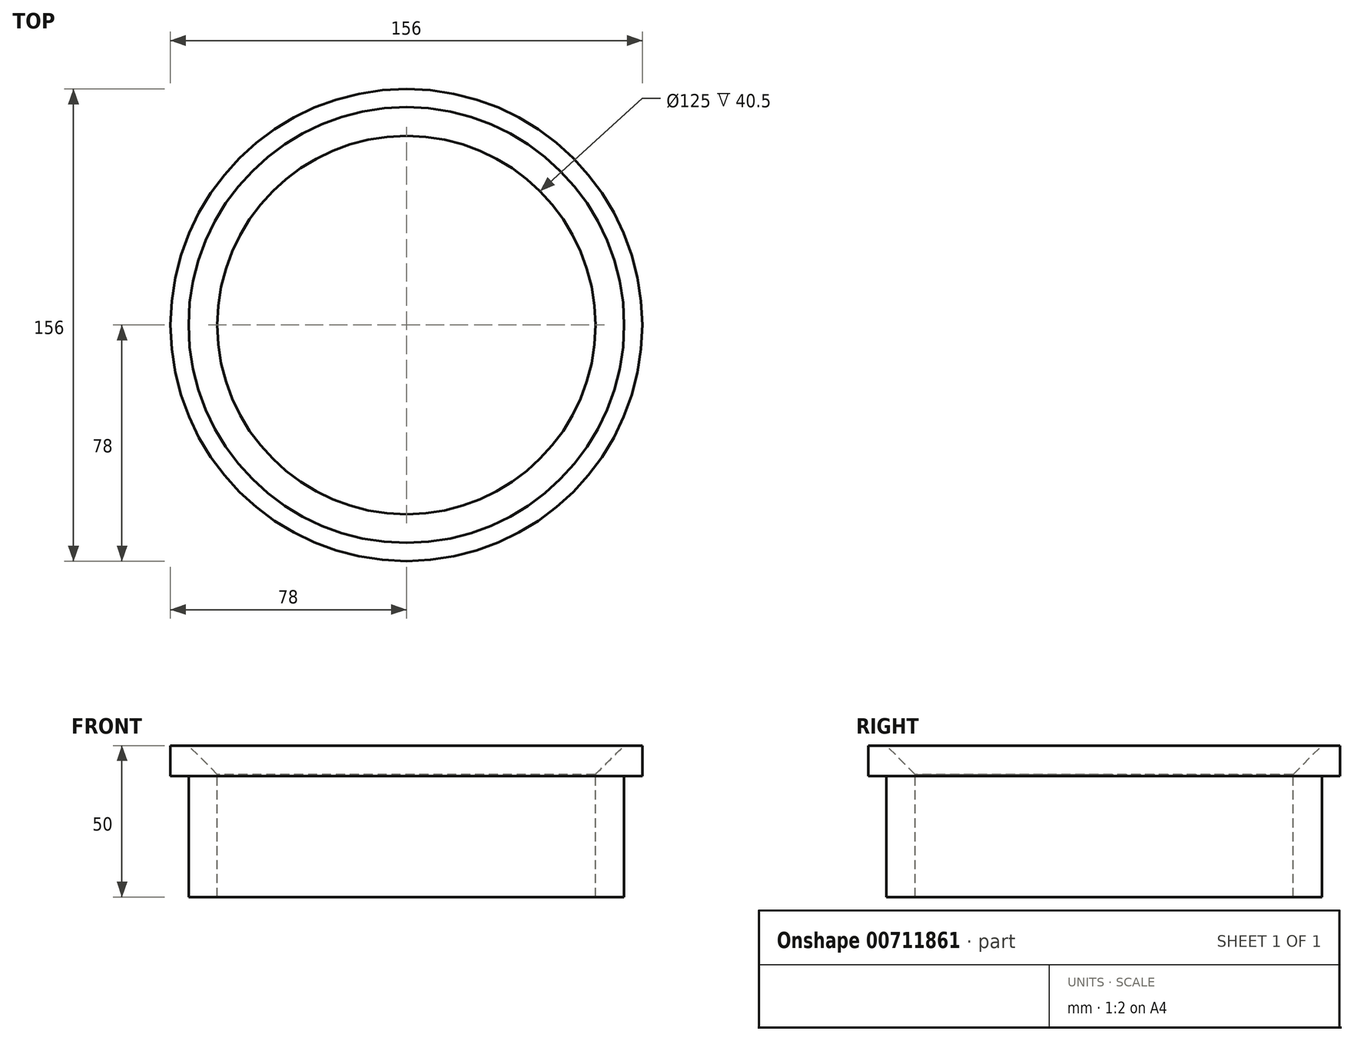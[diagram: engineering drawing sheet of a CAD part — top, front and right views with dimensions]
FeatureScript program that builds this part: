
annotation { "Feature Type Name" : "Feature", "Feature Type Description" : "" }
export const myFeature = defineFeature(function(context is Context, id is Id, definition is map)
    precondition{}
    {
        {
            var Q0;
            Q0=qCreatedBy(makeId("Front.planeOp"),FACE);
            var sketch = newSketch(context, id + "F0", { "sketchPlane" : qUnion([Q0])});
            skLineSegment(sketch, "E0", {"start": v(0, 50) * mm, "end": v(0, 0) * mm, "construction": true});
            skLineSegment(sketch, "E1", {"start": v(0, 0) * mm, "end": v(62.5, 0) * mm, "construction": true});
            skLineSegment(sketch, "E2", {"start": v(62.5, 0) * mm, "end": v(72, 0) * mm});
            skLineSegment(sketch, "E3", {"start": v(72, 0) * mm, "end": v(72, 40) * mm});
            skLineSegment(sketch, "E4", {"start": v(72, 40) * mm, "end": v(78, 40) * mm});
            skLineSegment(sketch, "E5", {"start": v(78, 40) * mm, "end": v(78, 50) * mm});
            skLineSegment(sketch, "E6", {"start": v(78, 50) * mm, "end": v(72, 50) * mm});
            skLineSegment(sketch, "E7", {"start": v(62.5, 40.5) * mm, "end": v(62.5, 0) * mm});
            skLineSegment(sketch, "E8", {"start": v(72, 50) * mm, "end": v(62.5, 40.5) * mm});
            skPoint(sketch, "E9.orphan", {"position": v(62.5, 50) * mm});
            skSolve(sketch);
        }
        {
            var Q0;
            Q0 = qSketchRegion(id + "F0", true);
            var Q1;
            Q1=sQuery(id+"F0.wireOp",EDGE,"E0");
            revolve(context, id + "F1", {"surfaceOperationType" : NewSurfaceOperationType.NEW, "entities" : qUnion([Q0]), "axis" : qUnion([Q1]), "revolveType" : RevolveType.FULL});
        }
    });
